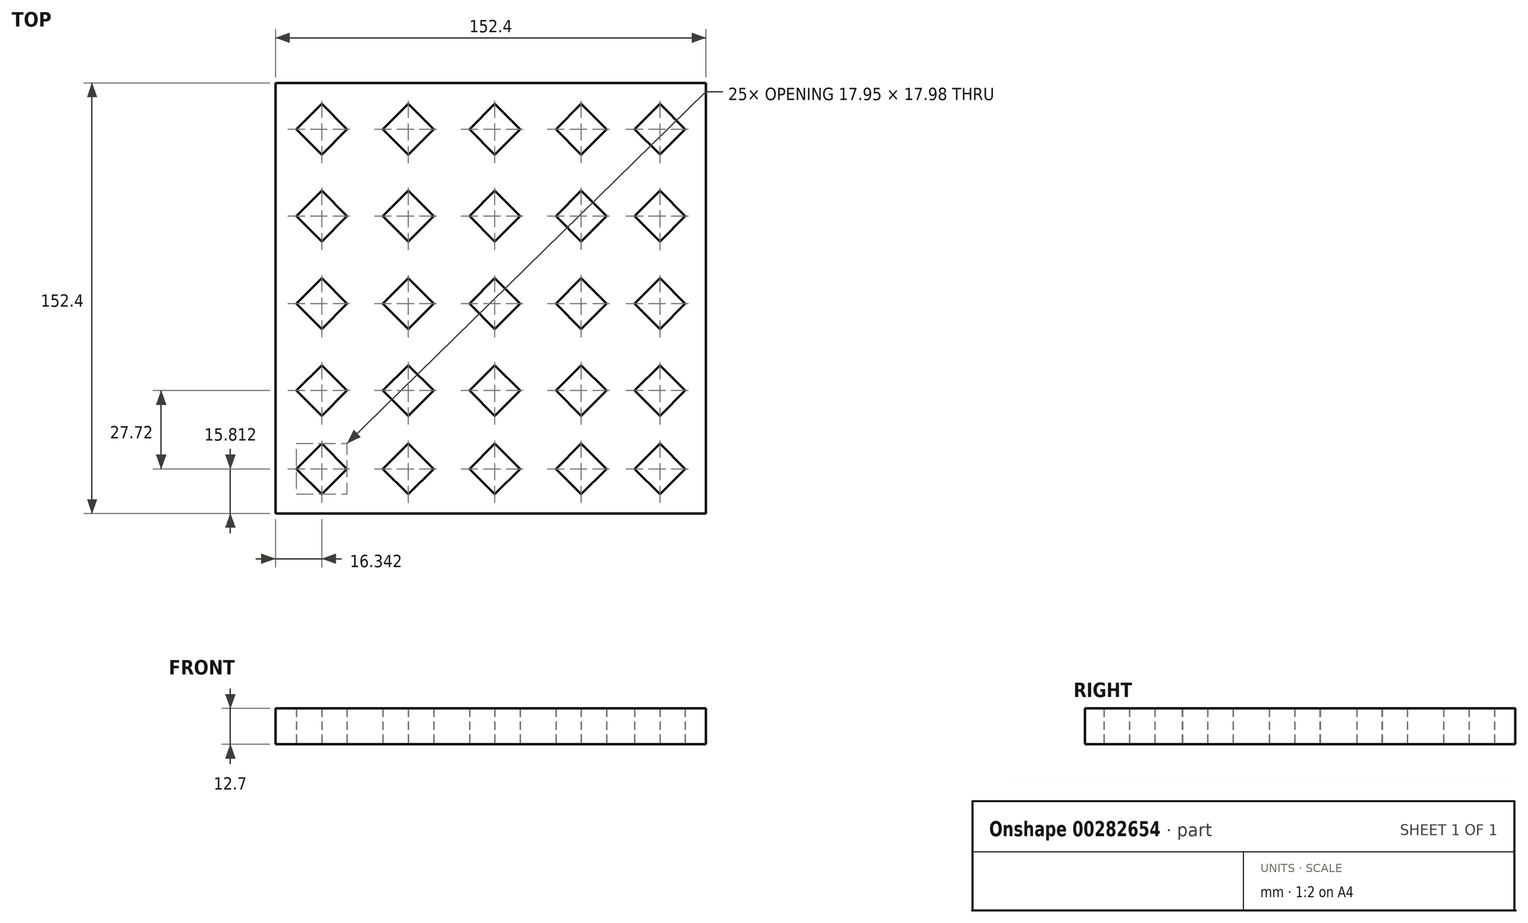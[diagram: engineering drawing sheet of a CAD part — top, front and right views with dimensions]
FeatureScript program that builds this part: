
annotation { "Feature Type Name" : "Feature", "Feature Type Description" : "" }
export const myFeature = defineFeature(function(context is Context, id is Id, definition is map)
    precondition{}
    {
        {
            var Q0;
            Q0=qCreatedBy(makeId("Top.planeOp"),FACE);
            var sketch = newSketch(context, id + "F0", { "sketchPlane" : qUnion([Q0])});
            skLineSegment(sketch, "E0.bottom", {"start": v(0, 0) * mm, "end": v(152.4, 0) * mm});
            skLineSegment(sketch, "E0.top", {"start": v(0, 152.4) * mm, "end": v(152.4, 152.4) * mm});
            skLineSegment(sketch, "E0.left", {"start": v(0, 0) * mm, "end": v(0, 152.4) * mm});
            skLineSegment(sketch, "E1", {"start": v(-67.22, -8.98) * mm, "end": v(-76.2, 0) * mm});
            skLineSegment(sketch, "E2", {"start": v(-76.2, 0) * mm, "end": v(-67.21, 8.98) * mm});
            skLineSegment(sketch, "E3", {"start": v(-67.21, 8.98) * mm, "end": v(-58.25, 0) * mm});
            skLineSegment(sketch, "E4", {"start": v(-58.25, 0) * mm, "end": v(-67.22, -8.98) * mm});
            skLineSegment(sketch, "E5", {"start": v(16.35, 127.06) * mm, "end": v(7.37, 136.04) * mm});
            skLineSegment(sketch, "E6", {"start": v(7.37, 136.04) * mm, "end": v(16.35, 145.02) * mm});
            skLineSegment(sketch, "E7", {"start": v(16.35, 145.02) * mm, "end": v(25.32, 136.05) * mm});
            skLineSegment(sketch, "E8", {"start": v(25.32, 136.05) * mm, "end": v(16.35, 127.06) * mm});
            skLineSegment(sketch, "E9.MirrorCS", {"start": v(7.37, 136.05) * mm, "end": v(16.35, 127.07) * mm});
            skLineSegment(sketch, "E10.MirrorCS", {"start": v(16.35, 127.07) * mm, "end": v(25.32, 136.05) * mm});
            skLineSegment(sketch, "E11.MirrorCS", {"start": v(25.32, 136.05) * mm, "end": v(16.35, 145.04) * mm});
            skLineSegment(sketch, "E12.MirrorCS", {"start": v(16.35, 145.04) * mm, "end": v(7.37, 136.05) * mm});
            skLineSegment(sketch, "E13.MirrorCS", {"start": v(46.98, 127.07) * mm, "end": v(38.02, 136.05) * mm});
            skLineSegment(sketch, "E14.MirrorCS", {"start": v(46.98, 145.02) * mm, "end": v(38.02, 136.05) * mm});
            skLineSegment(sketch, "E15.MirrorCS", {"start": v(55.97, 136.04) * mm, "end": v(46.98, 145.02) * mm});
            skLineSegment(sketch, "E16.MirrorCS", {"start": v(55.97, 136.05) * mm, "end": v(46.98, 127.07) * mm});
            skLineSegment(sketch, "E17.MirrorCS", {"start": v(38.02, 136.05) * mm, "end": v(46.99, 127.06) * mm});
            skLineSegment(sketch, "E18.MirrorCS", {"start": v(46.99, 127.06) * mm, "end": v(55.97, 136.04) * mm});
            skLineSegment(sketch, "E19.MirrorCS", {"start": v(38.02, 136.05) * mm, "end": v(46.99, 145.04) * mm});
            skLineSegment(sketch, "E20.MirrorCS", {"start": v(46.99, 145.04) * mm, "end": v(55.97, 136.05) * mm});
            skLineSegment(sketch, "E21.MirrorCS", {"start": v(68.67, 136.04) * mm, "end": v(77.65, 145.02) * mm});
            skLineSegment(sketch, "E22.MirrorCS", {"start": v(108.28, 145.02) * mm, "end": v(99.31, 136.05) * mm});
            skLineSegment(sketch, "E23.MirrorCS", {"start": v(77.65, 127.07) * mm, "end": v(86.61, 136.05) * mm});
            skLineSegment(sketch, "E24.MirrorCS", {"start": v(108.28, 127.07) * mm, "end": v(99.31, 136.05) * mm});
            skLineSegment(sketch, "E25.MirrorCS", {"start": v(117.26, 136.04) * mm, "end": v(108.28, 145.02) * mm});
            skLineSegment(sketch, "E26.MirrorCS", {"start": v(68.67, 136.05) * mm, "end": v(77.65, 127.07) * mm});
            skLineSegment(sketch, "E27.MirrorCS", {"start": v(108.29, 127.06) * mm, "end": v(117.26, 136.04) * mm});
            skLineSegment(sketch, "E28.MirrorCS", {"start": v(77.65, 145.02) * mm, "end": v(86.61, 136.05) * mm});
            skLineSegment(sketch, "E29.MirrorCS", {"start": v(86.61, 136.05) * mm, "end": v(77.64, 145.04) * mm});
            skLineSegment(sketch, "E30.MirrorCS", {"start": v(99.31, 136.05) * mm, "end": v(108.29, 127.06) * mm});
            skLineSegment(sketch, "E31.MirrorCS", {"start": v(117.26, 136.05) * mm, "end": v(108.28, 127.07) * mm});
            skLineSegment(sketch, "E32.MirrorCS", {"start": v(86.61, 136.05) * mm, "end": v(77.64, 127.06) * mm});
            skLineSegment(sketch, "E33.MirrorCS", {"start": v(77.64, 127.06) * mm, "end": v(68.67, 136.04) * mm});
            skLineSegment(sketch, "E34.MirrorCS", {"start": v(77.64, 145.04) * mm, "end": v(68.67, 136.05) * mm});
            skLineSegment(sketch, "E35.MirrorCS", {"start": v(99.31, 136.05) * mm, "end": v(108.29, 145.04) * mm});
            skLineSegment(sketch, "E36.MirrorCS", {"start": v(108.29, 145.04) * mm, "end": v(117.26, 136.05) * mm});
            skLineSegment(sketch, "E37.MirrorCS", {"start": v(136.13, 145.04) * mm, "end": v(127.16, 136.06) * mm});
            skLineSegment(sketch, "E38.MirrorCS", {"start": v(136.13, 127.1) * mm, "end": v(127.16, 136.06) * mm});
            skLineSegment(sketch, "E39.MirrorCS", {"start": v(145.11, 136.06) * mm, "end": v(136.13, 145.04) * mm});
            skLineSegment(sketch, "E40.MirrorCS", {"start": v(136.13, 127.07) * mm, "end": v(145.11, 136.06) * mm});
            skLineSegment(sketch, "E41.MirrorCS", {"start": v(127.16, 136.06) * mm, "end": v(136.13, 127.07) * mm});
            skLineSegment(sketch, "E42.MirrorCS", {"start": v(145.11, 136.07) * mm, "end": v(136.13, 127.1) * mm});
            skLineSegment(sketch, "E43.MirrorCS", {"start": v(127.16, 136.06) * mm, "end": v(136.13, 145.05) * mm});
            skLineSegment(sketch, "E44.MirrorCS", {"start": v(136.13, 145.05) * mm, "end": v(145.11, 136.07) * mm});
            skLineSegment(sketch, "E45.MirrorCS", {"start": v(16.35, 114.25) * mm, "end": v(25.32, 105.28) * mm});
            skLineSegment(sketch, "E46.MirrorCS", {"start": v(16.35, 114.27) * mm, "end": v(7.37, 105.28) * mm});
            skLineSegment(sketch, "E47.MirrorCS", {"start": v(77.65, 114.25) * mm, "end": v(86.61, 105.28) * mm});
            skLineSegment(sketch, "E48.MirrorCS", {"start": v(145.11, 105.26) * mm, "end": v(136.13, 96.29) * mm});
            skLineSegment(sketch, "E49.MirrorCS", {"start": v(16.35, 96.3) * mm, "end": v(25.32, 105.28) * mm});
            skLineSegment(sketch, "E50.MirrorCS", {"start": v(136.13, 114.23) * mm, "end": v(127.16, 105.26) * mm});
            skLineSegment(sketch, "E51.MirrorCS", {"start": v(117.26, 105.28) * mm, "end": v(108.28, 96.3) * mm});
            skLineSegment(sketch, "E52.MirrorCS", {"start": v(46.98, 114.25) * mm, "end": v(38.02, 105.28) * mm});
            skLineSegment(sketch, "E53.MirrorCS", {"start": v(108.28, 114.25) * mm, "end": v(99.31, 105.28) * mm});
            skLineSegment(sketch, "E54.MirrorCS", {"start": v(68.67, 105.27) * mm, "end": v(77.65, 114.25) * mm});
            skLineSegment(sketch, "E55.MirrorCS", {"start": v(136.13, 114.25) * mm, "end": v(145.11, 105.26) * mm});
            skLineSegment(sketch, "E56.MirrorCS", {"start": v(55.97, 105.27) * mm, "end": v(46.98, 114.25) * mm});
            skLineSegment(sketch, "E57.MirrorCS", {"start": v(117.26, 105.27) * mm, "end": v(108.28, 114.25) * mm});
            skLineSegment(sketch, "E58.MirrorCS", {"start": v(136.13, 96.29) * mm, "end": v(127.16, 105.26) * mm});
            skLineSegment(sketch, "E59.MirrorCS", {"start": v(77.65, 96.3) * mm, "end": v(86.61, 105.28) * mm});
            skLineSegment(sketch, "E60.MirrorCS", {"start": v(46.98, 96.3) * mm, "end": v(38.02, 105.28) * mm});
            skLineSegment(sketch, "E61.MirrorCS", {"start": v(99.31, 105.28) * mm, "end": v(108.29, 96.29) * mm});
            skLineSegment(sketch, "E62.MirrorCS", {"start": v(16.35, 96.29) * mm, "end": v(7.37, 105.27) * mm});
            skLineSegment(sketch, "E63.MirrorCS", {"start": v(7.37, 105.27) * mm, "end": v(16.35, 114.25) * mm});
            skLineSegment(sketch, "E64.MirrorCS", {"start": v(68.67, 105.28) * mm, "end": v(77.65, 96.3) * mm});
            skLineSegment(sketch, "E65.MirrorCS", {"start": v(55.97, 105.28) * mm, "end": v(46.98, 96.3) * mm});
            skLineSegment(sketch, "E66.MirrorCS", {"start": v(25.32, 105.28) * mm, "end": v(16.35, 96.29) * mm});
            skLineSegment(sketch, "E67.MirrorCS", {"start": v(145.11, 105.25) * mm, "end": v(136.13, 114.23) * mm});
            skLineSegment(sketch, "E68.MirrorCS", {"start": v(99.31, 105.28) * mm, "end": v(108.29, 114.27) * mm});
            skLineSegment(sketch, "E69.MirrorCS", {"start": v(127.16, 105.26) * mm, "end": v(136.13, 114.25) * mm});
            skLineSegment(sketch, "E70.MirrorCS", {"start": v(127.16, 105.26) * mm, "end": v(136.13, 96.27) * mm});
            skLineSegment(sketch, "E71.MirrorCS", {"start": v(108.29, 114.27) * mm, "end": v(117.26, 105.28) * mm});
            skLineSegment(sketch, "E72.MirrorCS", {"start": v(38.02, 105.28) * mm, "end": v(46.99, 96.29) * mm});
            skLineSegment(sketch, "E73.MirrorCS", {"start": v(7.37, 105.28) * mm, "end": v(16.35, 96.3) * mm});
            skLineSegment(sketch, "E74.MirrorCS", {"start": v(108.28, 96.3) * mm, "end": v(99.31, 105.28) * mm});
            skLineSegment(sketch, "E75.MirrorCS", {"start": v(25.32, 105.28) * mm, "end": v(16.35, 114.27) * mm});
            skLineSegment(sketch, "E76.MirrorCS", {"start": v(86.61, 105.28) * mm, "end": v(77.64, 114.27) * mm});
            skLineSegment(sketch, "E77.MirrorCS", {"start": v(136.13, 96.27) * mm, "end": v(145.11, 105.25) * mm});
            skLineSegment(sketch, "E78.MirrorCS", {"start": v(108.29, 96.29) * mm, "end": v(117.26, 105.27) * mm});
            skLineSegment(sketch, "E79.MirrorCS", {"start": v(77.64, 114.27) * mm, "end": v(68.67, 105.28) * mm});
            skLineSegment(sketch, "E80.MirrorCS", {"start": v(38.02, 105.28) * mm, "end": v(46.99, 114.27) * mm});
            skLineSegment(sketch, "E81.MirrorCS", {"start": v(77.64, 96.29) * mm, "end": v(68.67, 105.27) * mm});
            skLineSegment(sketch, "E82.MirrorCS", {"start": v(46.99, 96.29) * mm, "end": v(55.97, 105.27) * mm});
            skLineSegment(sketch, "E83.MirrorCS", {"start": v(46.99, 114.27) * mm, "end": v(55.97, 105.28) * mm});
            skLineSegment(sketch, "E84.MirrorCS", {"start": v(86.61, 105.28) * mm, "end": v(77.64, 96.29) * mm});
            skLineSegment(sketch, "E85.MirrorCS", {"start": v(16.35, 52.5) * mm, "end": v(25.32, 43.53) * mm});
            skLineSegment(sketch, "E86.MirrorCS", {"start": v(25.32, 43.53) * mm, "end": v(16.35, 34.54) * mm});
            skLineSegment(sketch, "E87.MirrorCS", {"start": v(145.11, 43.5) * mm, "end": v(136.13, 52.48) * mm});
            skLineSegment(sketch, "E88.MirrorCS", {"start": v(77.65, 52.5) * mm, "end": v(86.61, 43.53) * mm});
            skLineSegment(sketch, "E89.MirrorCS", {"start": v(99.31, 43.53) * mm, "end": v(108.29, 52.52) * mm});
            skLineSegment(sketch, "E90.MirrorCS", {"start": v(55.97, 43.53) * mm, "end": v(46.98, 52.5) * mm});
            skLineSegment(sketch, "E91.MirrorCS", {"start": v(77.64, 83.29) * mm, "end": v(68.67, 74.3) * mm});
            skLineSegment(sketch, "E92.MirrorCS", {"start": v(108.28, 65.33) * mm, "end": v(99.31, 74.3) * mm});
            skLineSegment(sketch, "E93.MirrorCS", {"start": v(117.26, 74.3) * mm, "end": v(108.28, 83.27) * mm});
            skLineSegment(sketch, "E94.MirrorCS", {"start": v(127.16, 43.51) * mm, "end": v(136.13, 34.52) * mm});
            skLineSegment(sketch, "E95.MirrorCS", {"start": v(99.31, 43.53) * mm, "end": v(108.29, 34.54) * mm});
            skLineSegment(sketch, "E96.MirrorCS", {"start": v(38.02, 43.53) * mm, "end": v(46.99, 34.54) * mm});
            skLineSegment(sketch, "E97.MirrorCS", {"start": v(77.65, 65.33) * mm, "end": v(86.61, 74.3) * mm});
            skLineSegment(sketch, "E98.MirrorCS", {"start": v(136.13, 83.29) * mm, "end": v(127.16, 74.32) * mm});
            skLineSegment(sketch, "E99.MirrorCS", {"start": v(145.11, 74.32) * mm, "end": v(136.13, 65.35) * mm});
            skLineSegment(sketch, "E100.MirrorCS", {"start": v(16.35, 34.54) * mm, "end": v(7.37, 43.53) * mm});
            skLineSegment(sketch, "E101.MirrorCS", {"start": v(108.29, 34.54) * mm, "end": v(117.26, 43.53) * mm});
            skLineSegment(sketch, "E102.MirrorCS", {"start": v(136.13, 34.52) * mm, "end": v(145.11, 43.5) * mm});
            skLineSegment(sketch, "E103.MirrorCS", {"start": v(68.67, 43.54) * mm, "end": v(77.65, 34.56) * mm});
            skLineSegment(sketch, "E104.MirrorCS", {"start": v(46.99, 34.54) * mm, "end": v(55.97, 43.53) * mm});
            skLineSegment(sketch, "E105.MirrorCS", {"start": v(46.99, 83.29) * mm, "end": v(55.97, 74.3) * mm});
            skLineSegment(sketch, "E106.MirrorCS", {"start": v(127.16, 74.32) * mm, "end": v(136.13, 65.33) * mm});
            skLineSegment(sketch, "E107.MirrorCS", {"start": v(77.65, 83.27) * mm, "end": v(86.61, 74.3) * mm});
            skLineSegment(sketch, "E108.MirrorCS", {"start": v(7.37, 43.53) * mm, "end": v(16.35, 52.5) * mm});
            skLineSegment(sketch, "E109.MirrorCS", {"start": v(136.13, 52.48) * mm, "end": v(127.16, 43.51) * mm});
            skLineSegment(sketch, "E110.MirrorCS", {"start": v(117.26, 43.53) * mm, "end": v(108.28, 52.5) * mm});
            skLineSegment(sketch, "E111.MirrorCS", {"start": v(16.35, 83.27) * mm, "end": v(25.32, 74.3) * mm});
            skLineSegment(sketch, "E112.MirrorCS", {"start": v(55.97, 74.3) * mm, "end": v(46.98, 65.33) * mm});
            skLineSegment(sketch, "E113.MirrorCS", {"start": v(46.98, 83.27) * mm, "end": v(38.02, 74.3) * mm});
            skLineSegment(sketch, "E114.MirrorCS", {"start": v(46.98, 52.5) * mm, "end": v(38.02, 43.53) * mm});
            skLineSegment(sketch, "E115.MirrorCS", {"start": v(99.31, 74.3) * mm, "end": v(108.29, 83.29) * mm});
            skLineSegment(sketch, "E116.MirrorCS", {"start": v(16.35, 65.33) * mm, "end": v(25.32, 74.3) * mm});
            skLineSegment(sketch, "E117.MirrorCS", {"start": v(16.35, 83.29) * mm, "end": v(7.37, 74.3) * mm});
            skLineSegment(sketch, "E118.MirrorCS", {"start": v(16.35, 65.31) * mm, "end": v(7.37, 74.3) * mm});
            skLineSegment(sketch, "E119.MirrorCS", {"start": v(68.67, 43.53) * mm, "end": v(77.65, 52.5) * mm});
            skLineSegment(sketch, "E120.MirrorCS", {"start": v(145.11, 74.31) * mm, "end": v(136.13, 83.29) * mm});
            skLineSegment(sketch, "E121.MirrorCS", {"start": v(77.65, 34.56) * mm, "end": v(86.61, 43.53) * mm});
            skLineSegment(sketch, "E122.MirrorCS", {"start": v(38.02, 74.3) * mm, "end": v(46.99, 65.31) * mm});
            skLineSegment(sketch, "E123.MirrorCS", {"start": v(77.64, 65.31) * mm, "end": v(68.67, 74.3) * mm});
            skLineSegment(sketch, "E124.MirrorCS", {"start": v(117.26, 74.3) * mm, "end": v(108.28, 65.33) * mm});
            skLineSegment(sketch, "E125.MirrorCS", {"start": v(68.67, 74.3) * mm, "end": v(77.65, 83.27) * mm});
            skLineSegment(sketch, "E126.MirrorCS", {"start": v(108.28, 52.5) * mm, "end": v(99.31, 43.53) * mm});
            skLineSegment(sketch, "E127.MirrorCS", {"start": v(55.97, 43.54) * mm, "end": v(46.98, 34.56) * mm});
            skLineSegment(sketch, "E128.MirrorCS", {"start": v(127.16, 74.32) * mm, "end": v(136.13, 83.3) * mm});
            skLineSegment(sketch, "E129.MirrorCS", {"start": v(136.13, 65.35) * mm, "end": v(127.16, 74.32) * mm});
            skLineSegment(sketch, "E130.MirrorCS", {"start": v(108.28, 34.56) * mm, "end": v(99.31, 43.53) * mm});
            skLineSegment(sketch, "E131.MirrorCS", {"start": v(136.13, 34.54) * mm, "end": v(127.16, 43.51) * mm});
            skLineSegment(sketch, "E132.MirrorCS", {"start": v(46.99, 65.31) * mm, "end": v(55.97, 74.3) * mm});
            skLineSegment(sketch, "E133.MirrorCS", {"start": v(117.26, 43.54) * mm, "end": v(108.28, 34.56) * mm});
            skLineSegment(sketch, "E134.MirrorCS", {"start": v(46.98, 34.56) * mm, "end": v(38.02, 43.53) * mm});
            skLineSegment(sketch, "E135.MirrorCS", {"start": v(38.02, 74.3) * mm, "end": v(46.99, 83.29) * mm});
            skLineSegment(sketch, "E136.MirrorCS", {"start": v(86.61, 74.3) * mm, "end": v(77.64, 83.29) * mm});
            skLineSegment(sketch, "E137.MirrorCS", {"start": v(145.11, 43.52) * mm, "end": v(136.13, 34.54) * mm});
            skLineSegment(sketch, "E138.MirrorCS", {"start": v(7.37, 74.3) * mm, "end": v(16.35, 83.27) * mm});
            skLineSegment(sketch, "E139.MirrorCS", {"start": v(7.37, 74.3) * mm, "end": v(16.35, 65.33) * mm});
            skLineSegment(sketch, "E140.MirrorCS", {"start": v(136.13, 52.5) * mm, "end": v(145.11, 43.52) * mm});
            skLineSegment(sketch, "E141.MirrorCS", {"start": v(108.28, 83.27) * mm, "end": v(99.31, 74.3) * mm});
            skLineSegment(sketch, "E142.MirrorCS", {"start": v(16.35, 34.56) * mm, "end": v(25.32, 43.53) * mm});
            skLineSegment(sketch, "E143.MirrorCS", {"start": v(7.37, 43.54) * mm, "end": v(16.35, 34.56) * mm});
            skLineSegment(sketch, "E144.MirrorCS", {"start": v(55.97, 74.3) * mm, "end": v(46.98, 83.27) * mm});
            skLineSegment(sketch, "E145.MirrorCS", {"start": v(68.67, 74.3) * mm, "end": v(77.65, 65.33) * mm});
            skLineSegment(sketch, "E146.MirrorCS", {"start": v(16.35, 52.52) * mm, "end": v(7.37, 43.54) * mm});
            skLineSegment(sketch, "E147.MirrorCS", {"start": v(46.98, 65.33) * mm, "end": v(38.02, 74.3) * mm});
            skLineSegment(sketch, "E148.MirrorCS", {"start": v(25.32, 43.53) * mm, "end": v(16.35, 52.52) * mm});
            skLineSegment(sketch, "E149.MirrorCS", {"start": v(108.29, 83.29) * mm, "end": v(117.26, 74.3) * mm});
            skLineSegment(sketch, "E150.MirrorCS", {"start": v(25.32, 74.3) * mm, "end": v(16.35, 65.31) * mm});
            skLineSegment(sketch, "E151.MirrorCS", {"start": v(77.64, 52.52) * mm, "end": v(68.67, 43.54) * mm});
            skLineSegment(sketch, "E152.MirrorCS", {"start": v(38.02, 43.53) * mm, "end": v(46.99, 52.52) * mm});
            skLineSegment(sketch, "E153.MirrorCS", {"start": v(127.16, 43.51) * mm, "end": v(136.13, 52.5) * mm});
            skLineSegment(sketch, "E154.MirrorCS", {"start": v(108.29, 52.52) * mm, "end": v(117.26, 43.54) * mm});
            skLineSegment(sketch, "E155.MirrorCS", {"start": v(46.99, 52.52) * mm, "end": v(55.97, 43.54) * mm});
            skLineSegment(sketch, "E156.MirrorCS", {"start": v(86.61, 43.53) * mm, "end": v(77.64, 34.54) * mm});
            skLineSegment(sketch, "E157.MirrorCS", {"start": v(136.13, 65.33) * mm, "end": v(145.11, 74.31) * mm});
            skLineSegment(sketch, "E158.MirrorCS", {"start": v(108.29, 65.31) * mm, "end": v(117.26, 74.3) * mm});
            skLineSegment(sketch, "E159.MirrorCS", {"start": v(25.32, 74.3) * mm, "end": v(16.35, 83.29) * mm});
            skLineSegment(sketch, "E160.MirrorCS", {"start": v(136.13, 83.3) * mm, "end": v(145.11, 74.32) * mm});
            skLineSegment(sketch, "E161.MirrorCS", {"start": v(86.61, 74.3) * mm, "end": v(77.64, 65.31) * mm});
            skLineSegment(sketch, "E162.MirrorCS", {"start": v(99.31, 74.3) * mm, "end": v(108.29, 65.31) * mm});
            skLineSegment(sketch, "E163.MirrorCS", {"start": v(86.61, 43.53) * mm, "end": v(77.64, 52.52) * mm});
            skLineSegment(sketch, "E164.MirrorCS", {"start": v(77.64, 34.54) * mm, "end": v(68.67, 43.53) * mm});
            skLineSegment(sketch, "E165.MirrorCS", {"start": v(16.35, 24.78) * mm, "end": v(25.32, 15.81) * mm});
            skLineSegment(sketch, "E166.MirrorCS", {"start": v(25.32, 15.81) * mm, "end": v(16.35, 6.82) * mm});
            skLineSegment(sketch, "E167.MirrorCS", {"start": v(145.11, 15.79) * mm, "end": v(136.13, 24.76) * mm});
            skLineSegment(sketch, "E168.MirrorCS", {"start": v(77.65, 24.78) * mm, "end": v(86.61, 15.81) * mm});
            skLineSegment(sketch, "E169.MirrorCS", {"start": v(99.31, 15.81) * mm, "end": v(108.29, 24.8) * mm});
            skLineSegment(sketch, "E170.MirrorCS", {"start": v(55.97, 15.8) * mm, "end": v(46.98, 24.78) * mm});
            skLineSegment(sketch, "E171.MirrorCS", {"start": v(127.16, 15.8) * mm, "end": v(136.13, 6.8) * mm});
            skLineSegment(sketch, "E172.MirrorCS", {"start": v(99.31, 15.81) * mm, "end": v(108.29, 6.82) * mm});
            skLineSegment(sketch, "E173.MirrorCS", {"start": v(38.02, 15.81) * mm, "end": v(46.99, 6.82) * mm});
            skLineSegment(sketch, "E174.MirrorCS", {"start": v(16.35, 6.82) * mm, "end": v(7.37, 15.8) * mm});
            skLineSegment(sketch, "E175.MirrorCS", {"start": v(108.29, 6.82) * mm, "end": v(117.26, 15.8) * mm});
            skLineSegment(sketch, "E176.MirrorCS", {"start": v(136.13, 6.8) * mm, "end": v(145.11, 15.79) * mm});
            skLineSegment(sketch, "E177.MirrorCS", {"start": v(68.67, 15.82) * mm, "end": v(77.65, 6.84) * mm});
            skLineSegment(sketch, "E178.MirrorCS", {"start": v(46.99, 6.82) * mm, "end": v(55.97, 15.8) * mm});
            skLineSegment(sketch, "E179.MirrorCS", {"start": v(7.37, 15.8) * mm, "end": v(16.35, 24.78) * mm});
            skLineSegment(sketch, "E180.MirrorCS", {"start": v(136.13, 24.76) * mm, "end": v(127.16, 15.8) * mm});
            skLineSegment(sketch, "E181.MirrorCS", {"start": v(117.26, 15.8) * mm, "end": v(108.28, 24.78) * mm});
            skLineSegment(sketch, "E182.MirrorCS", {"start": v(46.98, 24.78) * mm, "end": v(38.02, 15.81) * mm});
            skLineSegment(sketch, "E183.MirrorCS", {"start": v(68.67, 15.8) * mm, "end": v(77.65, 24.78) * mm});
            skLineSegment(sketch, "E184.MirrorCS", {"start": v(77.65, 6.84) * mm, "end": v(86.61, 15.81) * mm});
            skLineSegment(sketch, "E185.MirrorCS", {"start": v(108.28, 24.78) * mm, "end": v(99.31, 15.81) * mm});
            skLineSegment(sketch, "E186.MirrorCS", {"start": v(55.97, 15.82) * mm, "end": v(46.98, 6.84) * mm});
            skLineSegment(sketch, "E187.MirrorCS", {"start": v(108.28, 6.84) * mm, "end": v(99.31, 15.81) * mm});
            skLineSegment(sketch, "E188.MirrorCS", {"start": v(136.13, 6.82) * mm, "end": v(127.16, 15.8) * mm});
            skLineSegment(sketch, "E189.MirrorCS", {"start": v(117.26, 15.82) * mm, "end": v(108.28, 6.84) * mm});
            skLineSegment(sketch, "E190.MirrorCS", {"start": v(46.98, 6.84) * mm, "end": v(38.02, 15.81) * mm});
            skLineSegment(sketch, "E191.MirrorCS", {"start": v(145.11, 15.8) * mm, "end": v(136.13, 6.82) * mm});
            skLineSegment(sketch, "E192.MirrorCS", {"start": v(136.13, 24.78) * mm, "end": v(145.11, 15.8) * mm});
            skLineSegment(sketch, "E193.MirrorCS", {"start": v(16.35, 6.84) * mm, "end": v(25.32, 15.81) * mm});
            skLineSegment(sketch, "E194.MirrorCS", {"start": v(7.37, 15.82) * mm, "end": v(16.35, 6.84) * mm});
            skLineSegment(sketch, "E195.MirrorCS", {"start": v(16.35, 24.8) * mm, "end": v(7.37, 15.82) * mm});
            skLineSegment(sketch, "E196.MirrorCS", {"start": v(25.32, 15.81) * mm, "end": v(16.35, 24.8) * mm});
            skLineSegment(sketch, "E197.MirrorCS", {"start": v(77.64, 24.8) * mm, "end": v(68.67, 15.82) * mm});
            skLineSegment(sketch, "E198.MirrorCS", {"start": v(38.02, 15.81) * mm, "end": v(46.99, 24.8) * mm});
            skLineSegment(sketch, "E199.MirrorCS", {"start": v(127.16, 15.8) * mm, "end": v(136.13, 24.78) * mm});
            skLineSegment(sketch, "E200.MirrorCS", {"start": v(108.29, 24.8) * mm, "end": v(117.26, 15.82) * mm});
            skLineSegment(sketch, "E201.MirrorCS", {"start": v(46.99, 24.8) * mm, "end": v(55.97, 15.82) * mm});
            skLineSegment(sketch, "E202.MirrorCS", {"start": v(86.61, 15.81) * mm, "end": v(77.64, 6.82) * mm});
            skLineSegment(sketch, "E203.MirrorCS", {"start": v(86.61, 15.81) * mm, "end": v(77.64, 24.8) * mm});
            skLineSegment(sketch, "E204.MirrorCS", {"start": v(77.64, 6.82) * mm, "end": v(68.67, 15.8) * mm});
            skLineSegment(sketch, "E205", {"start": v(152.4, 152.4) * mm, "end": v(152.4, 0) * mm});
            skSolve(sketch);
        }
        {
            var Q0;
            Q0=makeQuery(id+"F0.imprint","IMPRINT",FACE,{"disambiguationData":[TD([[makeQuery(id+"F0.imprint","IMPRINT",EDGE,{"derivedFrom":sQuery(id+"F0.wireOp",EDGE,"E0.bottom")}),1.0]])]});
            extrude(context, id + "F1", {"entities" : qUnion([Q0]), "depth" : 12.7 * mm});
        }
    });
